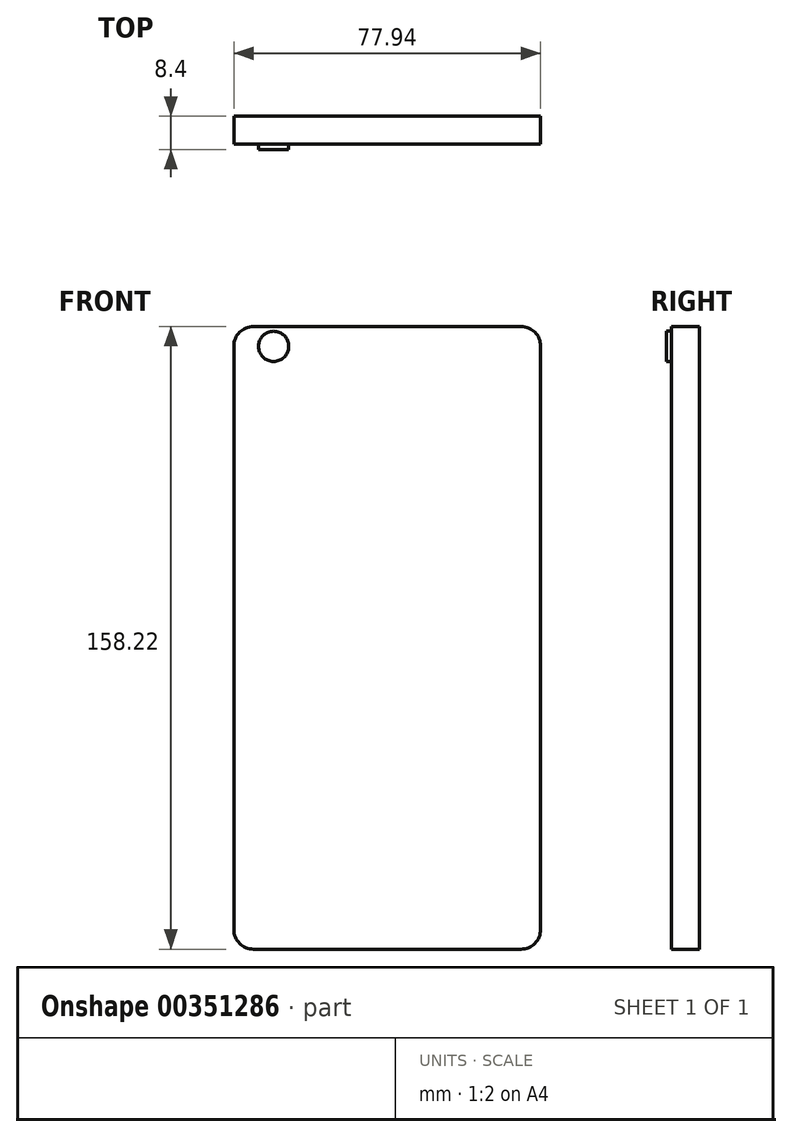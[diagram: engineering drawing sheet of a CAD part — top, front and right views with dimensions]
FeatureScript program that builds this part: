
annotation { "Feature Type Name" : "Feature", "Feature Type Description" : "" }
export const myFeature = defineFeature(function(context is Context, id is Id, definition is map)
    precondition{}
    {
        {
            var Q0;
            Q0=qCreatedBy(makeId("Front.planeOp"),FACE);
            var sketch = newSketch(context, id + "F0", { "sketchPlane" : qUnion([Q0])});
            skLineSegment(sketch, "E0", {"start": v(-52.23, 79.15) * mm, "end": v(-52.23, -69.07) * mm});
            skLineSegment(sketch, "E1", {"start": v(-47.23, -74.07) * mm, "end": v(20.71, -74.07) * mm});
            skLineSegment(sketch, "E2", {"start": v(25.71, -69.07) * mm, "end": v(25.71, 79.15) * mm});
            skLineSegment(sketch, "E3", {"start": v(20.71, 84.15) * mm, "end": v(-47.23, 84.15) * mm});
            skPoint(sketch, "E4.visualSharp", {"position": v(-52.23, 84.15) * mm});
            skArc(sketch, "E4.filletArc", {"start": v(-47.23, 84.15) * mm, "mid": v(-50.76, 82.68) * mm, "end": v(-52.23, 79.15) * mm});
            skArc(sketch, "E5.filletArc", {"start": v(-52.23, -69.07) * mm, "mid": v(-50.76, -72.6) * mm, "end": v(-47.23, -74.07) * mm});
            skPoint(sketch, "E6.visualSharp", {"position": v(25.71, -74.07) * mm});
            skArc(sketch, "E6.filletArc", {"start": v(20.71, -74.07) * mm, "mid": v(24.25, -72.6) * mm, "end": v(25.71, -69.07) * mm});
            skPoint(sketch, "E7.visualSharp", {"position": v(25.71, 84.15) * mm});
            skArc(sketch, "E7.filletArc", {"start": v(25.71, 79.15) * mm, "mid": v(24.25, 82.68) * mm, "end": v(20.71, 84.15) * mm});
            skPoint(sketch, "E8.startSnap0", {"position": v(-50.76, 82.68) * mm});
            skPoint(sketch, "E9.visualSharp", {"position": v(24.25, 82.68) * mm});
            skPoint(sketch, "E10.visualSharp", {"position": v(-50.76, -72.6) * mm});
            skPoint(sketch, "E11.visualSharp", {"position": v(24.25, -72.6) * mm});
            skCircle(sketch, "E12", {"center": v(-30.05, 79.05) * mm, "radius": 2.06 * mm});
            skCircle(sketch, "E13", {"center": v(-42.1, 79.1) * mm, "radius": 3.83 * mm});
            skLineSegment(sketch, "E14", {"start": v(-52.23, 74.18) * mm, "end": v(-24.6, 74.18) * mm});
            skLineSegment(sketch, "E15", {"start": v(-24.6, 84.15) * mm, "end": v(-24.6, 74.18) * mm});
            skSolve(sketch);
        }
        {
            var Q0;
            Q0=makeQuery(id+"F0.imprint","IMPRINT",FACE,{"disambiguationData":[TD([[makeQuery(id+"F0.imprint","IMPRINT",EDGE,{"derivedFrom":sQuery(id+"F0.wireOp",EDGE,"E13")}),1.0]])]});
            extrude(context, id + "F1", {"entities" : qUnion([Q0]), "depth" : 8.4 * mm});
        }
        {
            var Q0;
            Q0 = qSketchRegion(id + "F0", true);
            var Q1;
            Q1=makeQuery(id+"F0.imprint","IMPRINT",FACE,{"disambiguationData":[TD([[makeQuery(id+"F0.imprint","IMPRINT",EDGE,{"derivedFrom":sQuery(id+"F0.wireOp",EDGE,"E12")}),1.0]])]});
            extrude(context, id + "F2", {"entities" : qUnion([Q0, Q1]), "operationType" : NewBodyOperationType.ADD, "depth" : 7.1 * mm});
        }
    });
